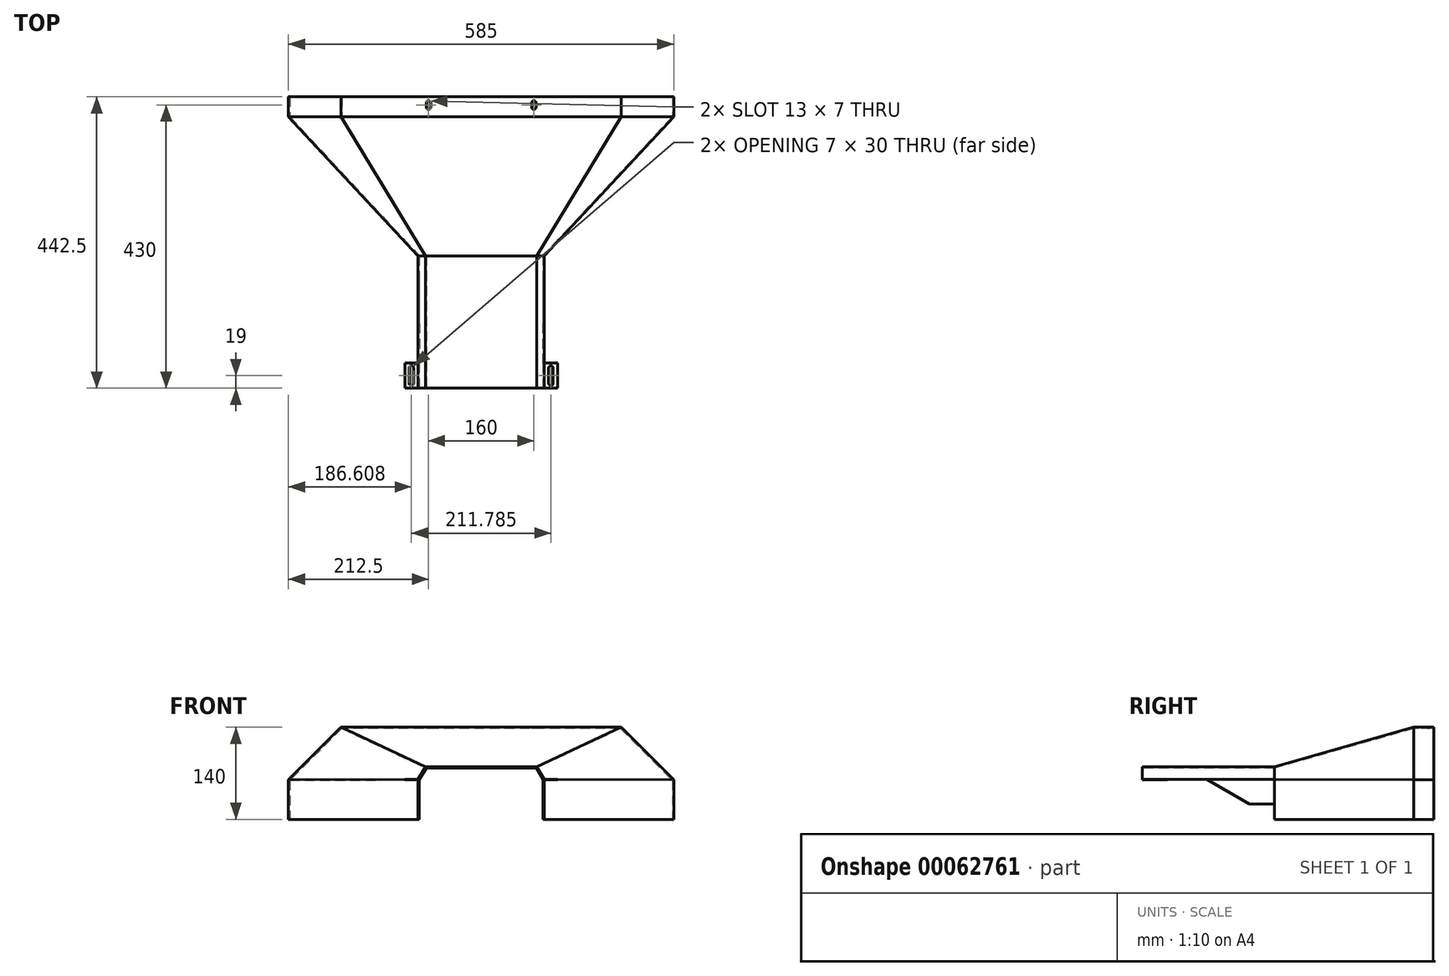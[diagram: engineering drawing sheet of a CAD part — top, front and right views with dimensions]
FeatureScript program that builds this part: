
annotation { "Feature Type Name" : "Feature", "Feature Type Description" : "" }
export const myFeature = defineFeature(function(context is Context, id is Id, definition is map)
    precondition{}
    {
        {
            var Q0;
            Q0=qCreatedBy(makeId("Front.planeOp"),FACE);
            var sketch = newSketch(context, id + "F0", { "sketchPlane" : qUnion([Q0])});
            skLineSegment(sketch, "E0", {"start": v(0, 78) * mm, "end": v(83.5, 78) * mm});
            skLineSegment(sketch, "E1", {"start": v(83.5, 78) * mm, "end": v(93.9, 60) * mm});
            skLineSegment(sketch, "E2", {"start": v(93.9, 60) * mm, "end": v(93.9, 0) * mm});
            skLineSegment(sketch, "E3", {"start": v(0, 78) * mm, "end": v(0, 0) * mm, "construction": true});
            skLineSegment(sketch, "E4.MirrorCS", {"start": v(0, 78) * mm, "end": v(-83.5, 78) * mm});
            skLineSegment(sketch, "E5.MirrorCS", {"start": v(-83.5, 78) * mm, "end": v(-93.9, 60) * mm});
            skLineSegment(sketch, "E6.MirrorCS", {"start": v(-93.9, 60) * mm, "end": v(-93.9, 0) * mm});
            skLineSegment(sketch, "E7.0", {"start": v(95.9, 60.54) * mm, "end": v(95.9, 0) * mm});
            skLineSegment(sketch, "E7.1", {"start": v(84.65, 80) * mm, "end": v(95.9, 60.54) * mm});
            skLineSegment(sketch, "E7.2", {"start": v(-95.9, 60.54) * mm, "end": v(-95.9, 0) * mm});
            skLineSegment(sketch, "E7.3", {"start": v(-84.65, 80) * mm, "end": v(-95.9, 60.54) * mm});
            skLineSegment(sketch, "E7.4", {"start": v(0, 80) * mm, "end": v(-84.65, 80) * mm});
            skLineSegment(sketch, "E7.5", {"start": v(0, 80) * mm, "end": v(84.65, 80) * mm});
            skLineSegment(sketch, "E8", {"start": v(95.9, 0) * mm, "end": v(93.9, 0) * mm});
            skLineSegment(sketch, "E9", {"start": v(-93.9, 0) * mm, "end": v(-95.9, 0) * mm});
            skSolve(sketch);
        }
        {
            var Q0;
            Q0=makeQuery(id+"F0.imprint","IMPRINT",FACE,{"disambiguationData":[TD([[makeQuery(id+"F0.imprint","IMPRINT",EDGE,{"derivedFrom":sQuery(id+"F0.wireOp",EDGE,"E0")}),1.0]])]});
            extrude(context, id + "F1", {"entities" : qUnion([Q0]), "oppositeDirection" : true, "depth" : 201 * mm});
        }
        {
            var Q0;
            Q0=qCreatedBy(makeId("Front.planeOp"),FACE);
            cPlane(context, id + "F2", {"entities" : qUnion([Q0]), "cplaneType" : CPlaneType.OFFSET, "offset" : (201 + 211.5) * mm, "oppositeDirection" : true, "width" : 150 * mm, "height" : 150 * mm});
        }
        {
            var Q0;
            Q0=qCreatedBy(id+"F2.planeOp",FACE);
            var sketch = newSketch(context, id + "F3", { "sketchPlane" : qUnion([Q0])});
            skLineSegment(sketch, "E10", {"start": v(0, 140) * mm, "end": v(212.5, 140) * mm});
            skLineSegment(sketch, "E11", {"start": v(212.5, 140) * mm, "end": v(292.5, 60) * mm});
            skLineSegment(sketch, "E12", {"start": v(292.5, 60) * mm, "end": v(292.5, 0) * mm});
            skLineSegment(sketch, "E13", {"start": v(0, 140) * mm, "end": v(0, 0) * mm, "construction": true});
            skLineSegment(sketch, "E14.MirrorCS", {"start": v(0, 140) * mm, "end": v(-212.5, 140) * mm});
            skLineSegment(sketch, "E15.MirrorCS", {"start": v(-212.5, 140) * mm, "end": v(-292.5, 60) * mm});
            skLineSegment(sketch, "E16.MirrorCS", {"start": v(-292.5, 60) * mm, "end": v(-292.5, 0) * mm});
            skLineSegment(sketch, "E17.0", {"start": v(-290.5, 59.17) * mm, "end": v(-290.5, 0) * mm});
            skLineSegment(sketch, "E17.1", {"start": v(-211.67, 138) * mm, "end": v(-290.5, 59.17) * mm});
            skLineSegment(sketch, "E17.2", {"start": v(290.5, 59.17) * mm, "end": v(290.5, 0) * mm});
            skLineSegment(sketch, "E17.3", {"start": v(211.67, 138) * mm, "end": v(290.5, 59.17) * mm});
            skLineSegment(sketch, "E17.4", {"start": v(0, 138) * mm, "end": v(211.67, 138) * mm});
            skLineSegment(sketch, "E17.5", {"start": v(0, 138) * mm, "end": v(-211.67, 138) * mm});
            skLineSegment(sketch, "E18", {"start": v(-292.5, 0) * mm, "end": v(-290.5, 0) * mm});
            skLineSegment(sketch, "E19", {"start": v(290.5, 0) * mm, "end": v(292.5, 0) * mm});
            skSolve(sketch);
        }
        {
            var Q0;
            Q0=makeQuery(id+"F3.imprint","IMPRINT",FACE,{"disambiguationData":[TD([[makeQuery(id+"F3.imprint","IMPRINT",EDGE,{"derivedFrom":sQuery(id+"F3.wireOp",EDGE,"E10")}),-1.0]])]});
            extrude(context, id + "F4", {"entities" : qUnion([Q0]), "oppositeDirection" : true, "depth" : 30 * mm});
        }
        {
            var Q0;
            Q0=makeQuery(id+"F4.opExtrude","CAP_FACE",FACE,{"disambiguationData":[OSD([sQuery(id+"F3.wireOp",EDGE,"E10"),sQuery(id+"F3.wireOp",EDGE,"E11"),sQuery(id+"F3.wireOp",EDGE,"E12"),sQuery(id+"F3.wireOp",EDGE,"E14.MirrorCS"),sQuery(id+"F3.wireOp",EDGE,"E15.MirrorCS"),sQuery(id+"F3.wireOp",EDGE,"E16.MirrorCS"),sQuery(id+"F3.wireOp",EDGE,"E17.0"),sQuery(id+"F3.wireOp",EDGE,"E17.1"),sQuery(id+"F3.wireOp",EDGE,"E17.2"),sQuery(id+"F3.wireOp",EDGE,"E17.3"),sQuery(id+"F3.wireOp",EDGE,"E17.4"),sQuery(id+"F3.wireOp",EDGE,"E17.5"),sQuery(id+"F3.wireOp",EDGE,"E18"),sQuery(id+"F3.wireOp",EDGE,"E19")])],"isStart":true});
            var Q1;
            Q1=makeQuery(id+"F1.opExtrude","CAP_FACE",FACE,{"disambiguationData":[OSD([sQuery(id+"F0.wireOp",EDGE,"E0"),sQuery(id+"F0.wireOp",EDGE,"E1"),sQuery(id+"F0.wireOp",EDGE,"E2"),sQuery(id+"F0.wireOp",EDGE,"E4.MirrorCS"),sQuery(id+"F0.wireOp",EDGE,"E5.MirrorCS"),sQuery(id+"F0.wireOp",EDGE,"E6.MirrorCS"),sQuery(id+"F0.wireOp",EDGE,"E7.0"),sQuery(id+"F0.wireOp",EDGE,"E7.1"),sQuery(id+"F0.wireOp",EDGE,"E7.2"),sQuery(id+"F0.wireOp",EDGE,"E7.3"),sQuery(id+"F0.wireOp",EDGE,"E7.4"),sQuery(id+"F0.wireOp",EDGE,"E7.5"),sQuery(id+"F0.wireOp",EDGE,"E8"),sQuery(id+"F0.wireOp",EDGE,"E9")])],"isStart":false});
            loft(context, id + "F5", {"operationType" : NewBodyOperationType.ADD, "sheetProfilesArray" : [{ "sheetProfileEntities" : qUnion([Q0]) }, { "sheetProfileEntities" : qUnion([Q1]) }]});
        }
        {
            var Q0;
            Q0=makeQuery(id+"F1.opExtrude","SWEPT_FACE",FACE,{"disambiguationData":[OSD([sQuery(id+"F0.wireOp",EDGE,"E7.2")])]});
            var sketch = newSketch(context, id + "F6", { "sketchPlane" : qUnion([Q0])});
            skLineSegment(sketch, "E20", {"start": v(-201, 23) * mm, "end": v(-163, 23) * mm});
            skLineSegment(sketch, "E21", {"start": v(-163, 23) * mm, "end": v(-98, 60.53) * mm});
            skLineSegment(sketch, "E22", {"start": v(-98, 60.53) * mm, "end": v(-38, 60.54) * mm});
            skLineSegment(sketch, "E23", {"start": v(-38, 60.54) * mm, "end": v(-38, 59.92) * mm});
            skLineSegment(sketch, "E24", {"start": v(-201, 23) * mm, "end": v(-201, 0) * mm});
            skLineSegment(sketch, "E25", {"start": v(-201, 0) * mm, "end": v(0, 0) * mm});
            skLineSegment(sketch, "E26.trimOffspring", {"start": v(-38, 59.92) * mm, "end": v(0, 60) * mm});
            skPoint(sketch, "E27.0.start.orphan", {"position": v(-201, 60) * mm});
            skLineSegment(sketch, "E28", {"start": v(0, 60) * mm, "end": v(0, 0) * mm});
            skSolve(sketch);
        }
        {
            var Q0;
            Q0=qSketchRegion(id+"F6",true);
            extrude(context, id + "F7", {"entities" : qUnion([Q0]), "operationType" : NewBodyOperationType.REMOVE, "endBound" : BoundingType.THROUGH_ALL, "oppositeDirection" : true, "depth" : 25 * mm});
        }
        {
            var Q0;
            {var subQ0=sQuery(id+"F0.wireOp",EDGE,"E7.2");var subQ1=makeQuery(id+"F1.opExtrude","SWEPT_FACE",FACE,{"disambiguationData":[OSD([subQ0])]});Q0=makeQuery(id+"F7.boolean.opBoolean","SPLIT",FACE,{"disambiguationData":[TD([makeQuery(id+"F7.opExtrude","SWEPT_FACE",FACE,{"disambiguationData":[OSD([sQuery(id+"F6.wireOp",EDGE,"E26.trimOffspring")])]})])],"derivedFrom":subQ1});}
            var sketch = newSketch(context, id + "F8", { "sketchPlane" : qUnion([Q0])});
            skLineSegment(sketch, "E29.0.0", {"start": v(-38, 60.54) * mm, "end": v(-38, 59.92) * mm});
            skLineSegment(sketch, "E29.0.1", {"start": v(-38, 59.92) * mm, "end": v(0, 60) * mm});
            skLineSegment(sketch, "E29.0.2", {"start": v(0, 60) * mm, "end": v(0, 60.54) * mm});
            skLineSegment(sketch, "E29.0.3", {"start": v(0, 60.54) * mm, "end": v(-38, 60.54) * mm});
            skSolve(sketch);
        }
        {
            var Q0;
            Q0=qSketchRegion(id+"F8",true);
            extrude(context, id + "F9", {"entities" : qUnion([Q0]), "operationType" : NewBodyOperationType.ADD, "depth" : 20 * mm});
        }
        {
            var Q0;
            {var subQ0=sQuery(id+"F0.wireOp",EDGE,"E7.0");var subQ1=makeQuery(id+"F1.opExtrude","SWEPT_FACE",FACE,{"disambiguationData":[OSD([subQ0])]});Q0=makeQuery(id+"F7.boolean.opBoolean","SPLIT",FACE,{"disambiguationData":[TD([makeQuery(id+"F7.opExtrude","SWEPT_FACE",FACE,{"disambiguationData":[OSD([sQuery(id+"F6.wireOp",EDGE,"E26.trimOffspring")])]})])],"derivedFrom":subQ1});}
            var sketch = newSketch(context, id + "F10", { "sketchPlane" : qUnion([Q0])});
            skLineSegment(sketch, "E30.0.0", {"start": v(0, 60) * mm, "end": v(38, 59.92) * mm});
            skLineSegment(sketch, "E30.0.1", {"start": v(38, 59.92) * mm, "end": v(38, 60.54) * mm});
            skLineSegment(sketch, "E30.0.2", {"start": v(38, 60.54) * mm, "end": v(0, 60.54) * mm});
            skLineSegment(sketch, "E30.0.3", {"start": v(0, 60.54) * mm, "end": v(0, 60) * mm});
            skSolve(sketch);
        }
        {
            var Q0;
            Q0=qSketchRegion(id+"F10",true);
            extrude(context, id + "F11", {"entities" : qUnion([Q0]), "operationType" : NewBodyOperationType.ADD, "depth" : 20 * mm});
        }
        {
            var Q0;
            Q0=makeQuery(id+"F9.opExtrude","SWEPT_FACE",FACE,{"disambiguationData":[OSD([sQuery(id+"F8.wireOp",EDGE,"E29.0.3")])]});
            var sketch = newSketch(context, id + "F12", { "sketchPlane" : qUnion([Q0])});
            skLineSegment(sketch, "E31", {"start": v(-105.9, 38) * mm, "end": v(-105.9, 0) * mm, "construction": true});
            skLineSegment(sketch, "E32", {"start": v(-115.9, 19) * mm, "end": v(-95.9, 19) * mm, "construction": true});
            skCircle(sketch, "E33", {"center": v(-105.9, 30.5) * mm, "radius": 3.5 * mm, "construction": true});
            skCircle(sketch, "E34", {"center": v(-105.9, 7.5) * mm, "radius": 3.5 * mm, "construction": true});
            skLineSegment(sketch, "E35", {"start": v(-105.9, 30.5) * mm, "end": v(-105.9, 7.5) * mm, "construction": true});
            skPoint(sketch, "E36", {"position": v(-105.9, 19) * mm});
            skLineSegment(sketch, "E37", {"start": v(-109.4, 30.5) * mm, "end": v(-109.4, 7.5) * mm});
            skLineSegment(sketch, "E38", {"start": v(-102.4, 30.5) * mm, "end": v(-102.4, 7.5) * mm});
            skArc(sketch, "E39", {"start": v(-109.4, 30.5) * mm, "mid": v(-105.9, 34) * mm, "end": v(-102.4, 30.5) * mm});
            skArc(sketch, "E40", {"start": v(-109.4, 7.5) * mm, "mid": v(-105.9, 4) * mm, "end": v(-102.4, 7.5) * mm});
            skSolve(sketch);
        }
        {
            var Q0;
            Q0=makeQuery(id+"F12.imprint","IMPRINT",FACE,{"disambiguationData":[TD([[makeQuery(id+"F12.imprint","IMPRINT",EDGE,{"derivedFrom":sQuery(id+"F12.wireOp",EDGE,"E37")}),1.0]])]});
            extrude(context, id + "F13", {"entities" : qUnion([Q0]), "operationType" : NewBodyOperationType.REMOVE, "endBound" : BoundingType.THROUGH_ALL, "oppositeDirection" : true, "depth" : 25 * mm});
        }
        {
            var Q0;
            Q0=makeQuery(id+"F11.opExtrude","SWEPT_FACE",FACE,{"disambiguationData":[OSD([sQuery(id+"F10.wireOp",EDGE,"E30.0.2")])]});
            var sketch = newSketch(context, id + "F14", { "sketchPlane" : qUnion([Q0])});
            skLineSegment(sketch, "E41", {"start": v(105.9, 38) * mm, "end": v(105.9, 0) * mm, "construction": true});
            skLineSegment(sketch, "E42", {"start": v(115.9, 19) * mm, "end": v(95.9, 19) * mm, "construction": true});
            skCircle(sketch, "E43", {"center": v(105.9, 30.5) * mm, "radius": 3.5 * mm, "construction": true});
            skCircle(sketch, "E44", {"center": v(105.9, 7.5) * mm, "radius": 3.5 * mm, "construction": true});
            skLineSegment(sketch, "E45", {"start": v(105.9, 30.5) * mm, "end": v(105.9, 7.5) * mm, "construction": true});
            skPoint(sketch, "E46", {"position": v(105.9, 19) * mm});
            skLineSegment(sketch, "E47", {"start": v(102.4, 30.5) * mm, "end": v(102.4, 7.5) * mm});
            skLineSegment(sketch, "E48", {"start": v(109.4, 30.5) * mm, "end": v(109.4, 7.5) * mm});
            skArc(sketch, "E49", {"start": v(102.4, 30.5) * mm, "mid": v(105.9, 34) * mm, "end": v(109.4, 30.5) * mm});
            skArc(sketch, "E50", {"start": v(102.4, 7.5) * mm, "mid": v(105.9, 4) * mm, "end": v(109.4, 7.5) * mm});
            skSolve(sketch);
        }
        {
            var Q0;
            Q0=makeQuery(id+"F14.imprint","IMPRINT",FACE,{"disambiguationData":[TD([[makeQuery(id+"F14.imprint","IMPRINT",EDGE,{"derivedFrom":sQuery(id+"F14.wireOp",EDGE,"E47")}),1.0]])]});
            extrude(context, id + "F15", {"entities" : qUnion([Q0]), "operationType" : NewBodyOperationType.REMOVE, "endBound" : BoundingType.THROUGH_ALL, "oppositeDirection" : true, "depth" : 25 * mm});
        }
        {
            var Q0;
            Q0=makeQuery(id+"F4.opExtrude","SWEPT_FACE",FACE,{"disambiguationData":[OSD([sQuery(id+"F3.wireOp",EDGE,"E10"),sQuery(id+"F3.wireOp",EDGE,"E14.MirrorCS")])]});
            var sketch = newSketch(context, id + "F16", { "sketchPlane" : qUnion([Q0])});
            skLineSegment(sketch, "E51", {"start": v(0, 442.5) * mm, "end": v(0, 412.5) * mm, "construction": true});
            skCircle(sketch, "E52", {"center": v(80, 433) * mm, "radius": 3.5 * mm, "construction": true});
            skLineSegment(sketch, "E53", {"start": v(80, 433) * mm, "end": v(80, 427) * mm, "construction": true});
            skCircle(sketch, "E54", {"center": v(80, 427) * mm, "radius": 3.5 * mm, "construction": true});
            skLineSegment(sketch, "E55", {"start": v(83.5, 433) * mm, "end": v(83.5, 427) * mm});
            skLineSegment(sketch, "E56", {"start": v(76.5, 433) * mm, "end": v(76.5, 427) * mm});
            skArc(sketch, "E57", {"start": v(76.5, 433) * mm, "mid": v(80, 436.5) * mm, "end": v(83.5, 433) * mm});
            skArc(sketch, "E58", {"start": v(83.5, 427) * mm, "mid": v(80, 423.5) * mm, "end": v(76.5, 427) * mm});
            skPoint(sketch, "E59", {"position": v(80, 430) * mm});
            skLineSegment(sketch, "E60", {"start": v(0, 430) * mm, "end": v(212.5, 430) * mm, "construction": true});
            skArc(sketch, "E61.MirrorCS", {"start": v(-76.5, 433) * mm, "mid": v(-80, 436.5) * mm, "end": v(-83.5, 433) * mm});
            skLineSegment(sketch, "E62.MirrorCS", {"start": v(-83.5, 433) * mm, "end": v(-83.5, 427) * mm});
            skLineSegment(sketch, "E63.MirrorCS", {"start": v(-76.5, 433) * mm, "end": v(-76.5, 427) * mm});
            skArc(sketch, "E64.MirrorCS", {"start": v(-83.5, 427) * mm, "mid": v(-80, 423.5) * mm, "end": v(-76.5, 427) * mm});
            skSolve(sketch);
        }
        {
            var Q0;
            Q0=makeQuery(id+"F16.imprint","IMPRINT",FACE,{"disambiguationData":[TD([[makeQuery(id+"F16.imprint","IMPRINT",EDGE,{"derivedFrom":sQuery(id+"F16.wireOp",EDGE,"E61.MirrorCS")}),1.0]])]});
            var Q1;
            Q1=makeQuery(id+"F16.imprint","IMPRINT",FACE,{"disambiguationData":[TD([[makeQuery(id+"F16.imprint","IMPRINT",EDGE,{"derivedFrom":sQuery(id+"F16.wireOp",EDGE,"E55")}),-1.0]])]});
            extrude(context, id + "F17", {"entities" : qUnion([Q0, Q1]), "operationType" : NewBodyOperationType.REMOVE, "endBound" : BoundingType.THROUGH_ALL, "oppositeDirection" : true, "depth" : 25 * mm});
        }
        {
            var Q0;
            Q0=makeQuery(id+"F4.opExtrude","SWEPT_FACE",FACE,{"disambiguationData":[OSD([sQuery(id+"F3.wireOp",EDGE,"E15.MirrorCS")])]});
            var sketch = newSketch(context, id + "F18", { "sketchPlane" : qUnion([Q0])});
            skLineSegment(sketch, "E65", {"start": v(-164.4, 430) * mm, "end": v(-51.27, 430) * mm, "construction": true});
            skCircle(sketch, "E66", {"center": v(-120.27, 430) * mm, "radius": 6 * mm, "construction": true});
            skCircle(sketch, "E67", {"center": v(-102.27, 430) * mm, "radius": 6 * mm, "construction": true});
            skLineSegment(sketch, "E68", {"start": v(-120.27, 430) * mm, "end": v(-102.27, 430) * mm, "construction": true});
            skPoint(sketch, "E69", {"position": v(-111.27, 430) * mm});
            skLineSegment(sketch, "E70", {"start": v(-120.27, 436) * mm, "end": v(-102.27, 436) * mm});
            skLineSegment(sketch, "E71", {"start": v(-102.27, 424) * mm, "end": v(-120.27, 424) * mm});
            skArc(sketch, "E72", {"start": v(-120.27, 436) * mm, "mid": v(-126.27, 430) * mm, "end": v(-120.27, 424) * mm});
            skArc(sketch, "E73", {"start": v(-102.27, 424) * mm, "mid": v(-96.27, 430) * mm, "end": v(-102.27, 436) * mm});
            skSolve(sketch);
        }
        {
            var Q0;
            Q0=makeQuery(id+"F18.imprint","IMPRINT",FACE,{"disambiguationData":[TD([[makeQuery(id+"F18.imprint","IMPRINT",EDGE,{"derivedFrom":sQuery(id+"F18.wireOp",EDGE,"E70")}),-1.0]])]});
            extrude(context, id + "F19", {"entities" : qUnion([Q0]), "operationType" : NewBodyOperationType.REMOVE, "endBound" : BoundingType.THROUGH_ALL, "oppositeDirection" : true, "depth" : 25 * mm});
        }
        {
            var Q0;
            Q0=makeQuery(id+"F4.opExtrude","SWEPT_FACE",FACE,{"disambiguationData":[OSD([sQuery(id+"F3.wireOp",EDGE,"E11")])]});
            var sketch = newSketch(context, id + "F20", { "sketchPlane" : qUnion([Q0])});
            skLineSegment(sketch, "E74", {"start": v(51.27, 430) * mm, "end": v(164.4, 430) * mm, "construction": true});
            skCircle(sketch, "E75", {"center": v(102.27, 430) * mm, "radius": 6 * mm, "construction": true});
            skCircle(sketch, "E76", {"center": v(120.27, 430) * mm, "radius": 6 * mm, "construction": true});
            skLineSegment(sketch, "E77", {"start": v(120.27, 436) * mm, "end": v(102.27, 436) * mm});
            skLineSegment(sketch, "E78", {"start": v(102.27, 424) * mm, "end": v(120.27, 424) * mm});
            skLineSegment(sketch, "E79", {"start": v(102.27, 430) * mm, "end": v(120.27, 430) * mm, "construction": true});
            skPoint(sketch, "E80", {"position": v(111.27, 430) * mm});
            skArc(sketch, "E81", {"start": v(102.27, 436) * mm, "mid": v(96.27, 430) * mm, "end": v(102.27, 424) * mm});
            skArc(sketch, "E82", {"start": v(120.27, 424) * mm, "mid": v(126.27, 430) * mm, "end": v(120.27, 436) * mm});
            skSolve(sketch);
        }
        {
            var Q0;
            Q0=makeQuery(id+"F20.imprint","IMPRINT",FACE,{"disambiguationData":[TD([[makeQuery(id+"F20.imprint","IMPRINT",EDGE,{"derivedFrom":sQuery(id+"F20.wireOp",EDGE,"E77")}),1.0]])]});
            extrude(context, id + "F21", {"entities" : qUnion([Q0]), "operationType" : NewBodyOperationType.REMOVE, "endBound" : BoundingType.THROUGH_ALL, "oppositeDirection" : true, "depth" : 25 * mm});
        }
    });
